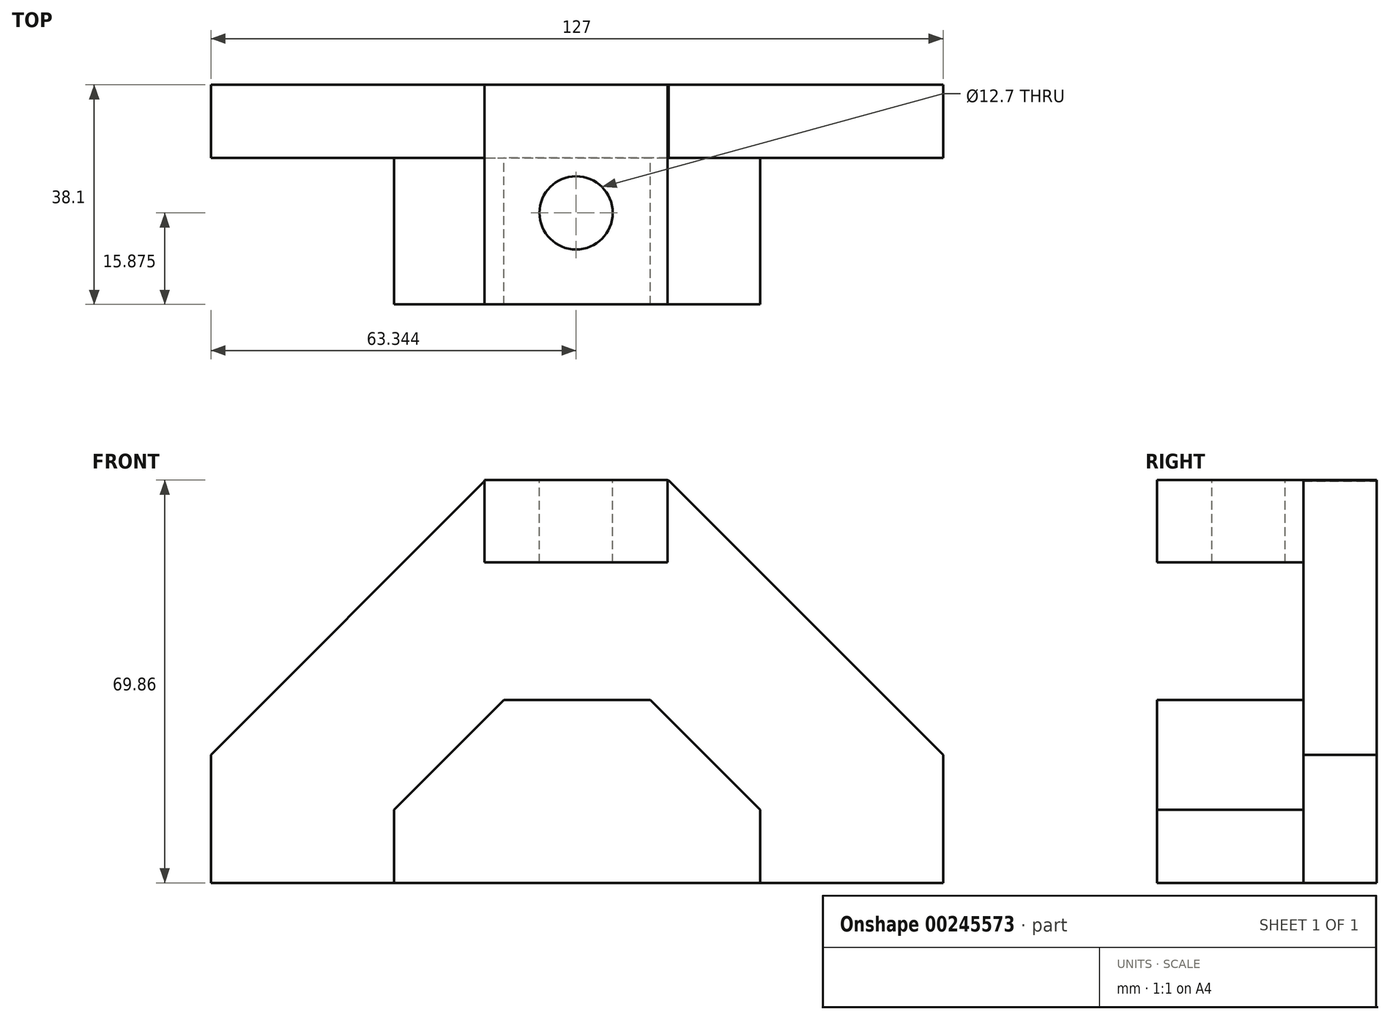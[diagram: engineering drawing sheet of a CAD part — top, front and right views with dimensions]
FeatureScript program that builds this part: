
annotation { "Feature Type Name" : "Feature", "Feature Type Description" : "" }
export const myFeature = defineFeature(function(context is Context, id is Id, definition is map)
    precondition{}
    {
        {
            var Q0;
            Q0=qCreatedBy(makeId("Front.planeOp"),FACE);
            var sketch = newSketch(context, id + "F0", { "sketchPlane" : qUnion([Q0])});
            skLineSegment(sketch, "E0.bottom", {"start": v(-74.19, -11.72) * mm, "end": v(52.81, -11.72) * mm});
            skLineSegment(sketch, "E0.top", {"start": v(-74.19, 58.13) * mm, "end": v(52.81, 58.13) * mm});
            skLineSegment(sketch, "E0.left", {"start": v(-74.19, -11.72) * mm, "end": v(-74.19, 58.13) * mm});
            skLineSegment(sketch, "E0.right", {"start": v(52.81, -11.72) * mm, "end": v(52.81, 58.13) * mm});
            skLineSegment(sketch, "E1", {"start": v(5.19, 58.13) * mm, "end": v(52.81, 10.5) * mm});
            skLineSegment(sketch, "E2", {"start": v(-26.56, 58.13) * mm, "end": v(-74.19, 10.5) * mm});
            skSolve(sketch);
        }
        {
            var Q0;
            {var subQ1=sQuery(id+"F0.wireOp",EDGE,"E0.bottom");Q0=makeQuery(id+"F0.imprint","IMPRINT",FACE,{"disambiguationData":[TD([[makeQuery(id+"F0.imprint","IMPRINT",EDGE,{"derivedFrom":subQ1}),1.0]])]});}
            extrude(context, id + "F1", {"entities" : qUnion([Q0]), "depth" : 12.7 * mm});
        }
        {
            var Q0;
            Q0=qCreatedBy(makeId("Front.planeOp"),FACE);
            var sketch = newSketch(context, id + "F2", { "sketchPlane" : qUnion([Q0])});
            skLineSegment(sketch, "E3.bottom", {"start": v(-42.44, -11.72) * mm, "end": v(21.06, -11.72) * mm});
            skLineSegment(sketch, "E3.top", {"start": v(-42.44, 20.03) * mm, "end": v(21.06, 20.03) * mm});
            skLineSegment(sketch, "E3.left", {"start": v(-42.44, -11.72) * mm, "end": v(-42.44, 20.03) * mm});
            skLineSegment(sketch, "E3.right", {"start": v(21.06, -11.72) * mm, "end": v(21.06, 20.03) * mm});
            skPoint(sketch, "E3.middle", {"position": v(-10.69, 4.16) * mm});
            skLineSegment(sketch, "E4", {"start": v(2.01, 20.03) * mm, "end": v(21.06, 0.98) * mm});
            skLineSegment(sketch, "E5", {"start": v(-23.39, 20.03) * mm, "end": v(-42.44, 0.98) * mm});
            skSolve(sketch);
        }
        {
            var Q0;
            {var subQ1=sQuery(id+"F2.wireOp",EDGE,"E3.bottom");Q0=makeQuery(id+"F2.imprint","IMPRINT",FACE,{"disambiguationData":[TD([[makeQuery(id+"F2.imprint","IMPRINT",EDGE,{"derivedFrom":subQ1}),1.0]])]});}
            extrude(context, id + "F3", {"entities" : qUnion([Q0]), "operationType" : NewBodyOperationType.ADD, "depth" : 38.1 * mm});
        }
        {
            var Q0;
            Q0=qCreatedBy(makeId("Front.planeOp"),FACE);
            var sketch = newSketch(context, id + "F4", { "sketchPlane" : qUnion([Q0])});
            skLineSegment(sketch, "E6.bottom", {"start": v(5.03, 43.86) * mm, "end": v(-26.72, 43.86) * mm});
            skLineSegment(sketch, "E6.top", {"start": v(5.03, 58.14) * mm, "end": v(-26.72, 58.14) * mm});
            skLineSegment(sketch, "E6.left", {"start": v(5.03, 43.86) * mm, "end": v(5.03, 58.14) * mm});
            skLineSegment(sketch, "E6.right", {"start": v(-26.72, 43.86) * mm, "end": v(-26.72, 58.14) * mm});
            skPoint(sketch, "E6.middle", {"position": v(-10.85, 51) * mm});
            skSolve(sketch);
        }
        {
            var Q0;
            Q0 = qSketchRegion(id + "F4", true);
            extrude(context, id + "F5", {"entities" : qUnion([Q0]), "operationType" : NewBodyOperationType.ADD, "depth" : 38.1 * mm});
        }
        {
            var Q0;
            Q0=makeQuery(id+"F5.opExtrude","SWEPT_FACE",FACE,{"disambiguationData":[OSD([sQuery(id+"F4.wireOp",EDGE,"E6.top")])]});
            var sketch = newSketch(context, id + "F6", { "sketchPlane" : qUnion([Q0])});
            skCircle(sketch, "E7", {"center": v(-10.85, -22.23) * mm, "radius": 6.35 * mm});
            skSolve(sketch);
        }
        {
            var Q0;
            Q0 = qSketchRegion(id + "F6", true);
            extrude(context, id + "F7", {"entities" : qUnion([Q0]), "operationType" : NewBodyOperationType.REMOVE, "oppositeDirection" : true, "depth" : 14.29 * mm});
        }
    });
